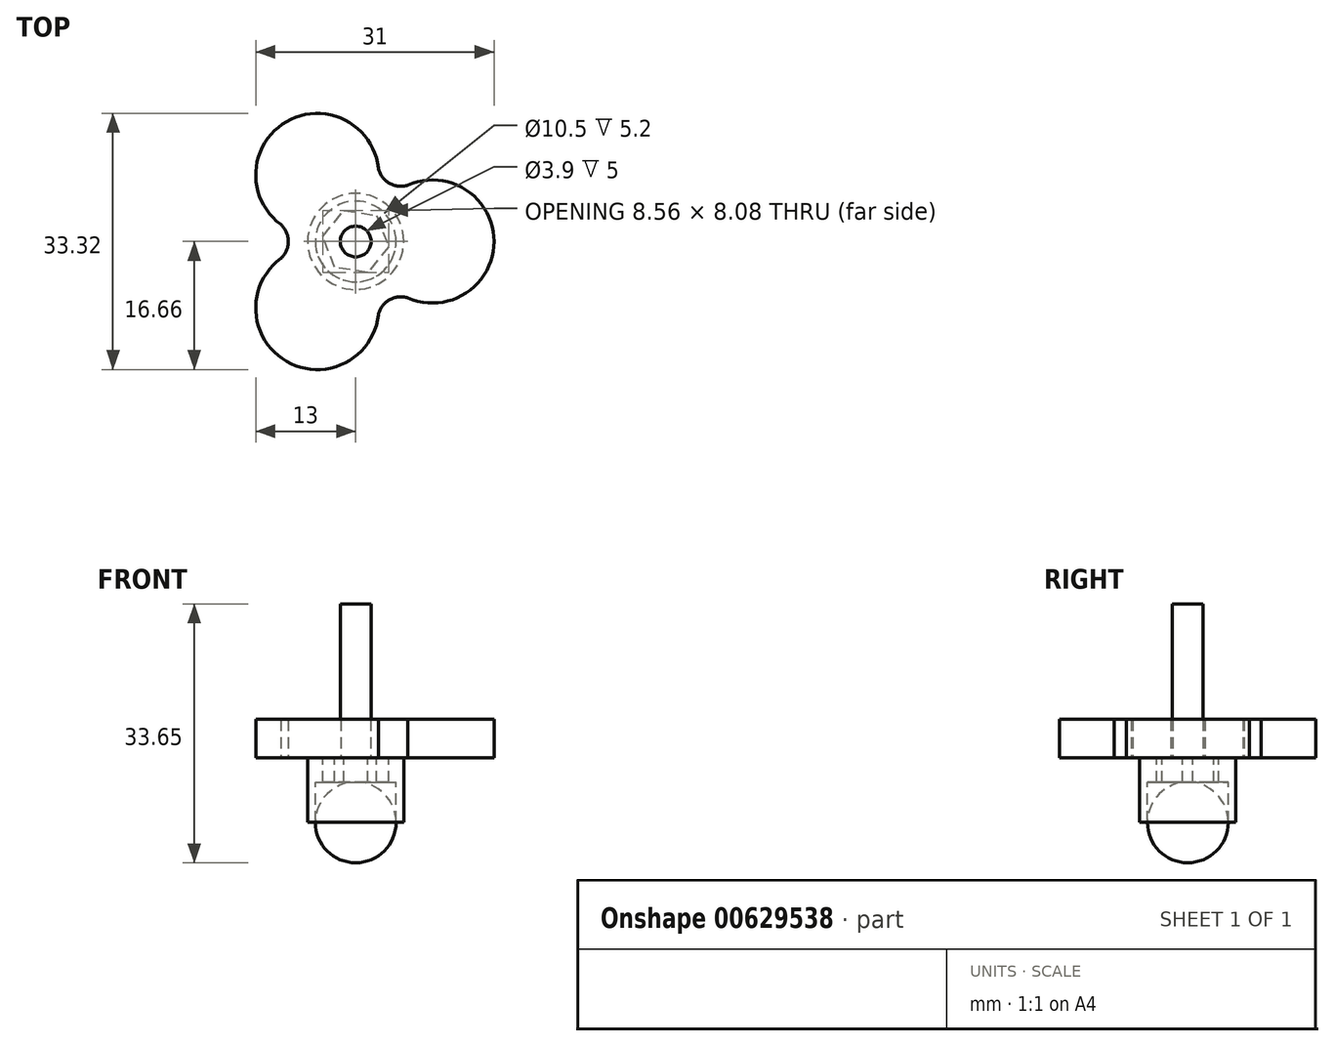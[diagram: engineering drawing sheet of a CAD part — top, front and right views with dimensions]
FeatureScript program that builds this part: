
annotation { "Feature Type Name" : "Feature", "Feature Type Description" : "" }
export const myFeature = defineFeature(function(context is Context, id is Id, definition is map)
    precondition{}
    {
        {
            var Q0;
            Q0=qCreatedBy(makeId("Top.planeOp"),FACE);
            var sketch = newSketch(context, id + "F0", { "sketchPlane" : qUnion([Q0])});
            skCircle(sketch, "E0", {"center": v(0, 0) * mm, "radius": 1.95 * mm});
            skArc(sketch, "E1", {"start": v(6.8, -7.33) * mm, "mid": v(18, 0) * mm, "end": v(6.8, 7.33) * mm});
            skArc(sketch, "E2", {"start": v(-9.75, -2.22) * mm, "mid": v(-9, -15.59) * mm, "end": v(2.95, -9.56) * mm});
            skArc(sketch, "E3.trimOffspring", {"start": v(2.95, 9.56) * mm, "mid": v(-9, 15.59) * mm, "end": v(-9.75, 2.22) * mm});
            skPoint(sketch, "E4", {"position": v(18, 0) * mm});
            skPoint(sketch, "E5", {"position": v(-9, 15.59) * mm});
            skPoint(sketch, "E6", {"position": v(-9, -15.59) * mm});
            skArc(sketch, "E7", {"start": v(-9.75, -2.22) * mm, "mid": v(-8.76, 0) * mm, "end": v(-9.75, 2.22) * mm});
            skArc(sketch, "E8", {"start": v(2.95, 9.56) * mm, "mid": v(4.38, 7.6) * mm, "end": v(6.8, 7.33) * mm});
            skArc(sketch, "E9", {"start": v(6.8, -7.33) * mm, "mid": v(4.38, -7.6) * mm, "end": v(2.95, -9.56) * mm});
            skSolve(sketch);
        }
        {
            var Q0;
            Q0 = qSketchRegion(id + "F0", true);
            extrude(context, id + "F1", {"entities" : qUnion([Q0]), "depth" : 5 * mm, "offsetDistance" : 25 * mm});
        }
        {
            var Q0;
            Q0=qCreatedBy(makeId("Top.planeOp"),FACE);
            var sketch = newSketch(context, id + "F2", { "sketchPlane" : qUnion([Q0])});
            skPoint(sketch, "E10.0.midPoint", {"position": v(2.46, -3.41) * mm});
            skCircle(sketch, "E11", {"center": v(0, 0) * mm, "radius": 6.25 * mm});
            skLineSegment(sketch, "E12.0", {"start": v(2.72, 3.37) * mm, "end": v(4.28, -0.67) * mm});
            skLineSegment(sketch, "E12.1", {"start": v(4.28, -0.67) * mm, "end": v(1.56, -4.04) * mm});
            skLineSegment(sketch, "E12.2", {"start": v(1.56, -4.04) * mm, "end": v(-2.72, -3.37) * mm});
            skLineSegment(sketch, "E12.3", {"start": v(-2.72, -3.37) * mm, "end": v(-4.28, 0.67) * mm});
            skLineSegment(sketch, "E12.4", {"start": v(-4.28, 0.67) * mm, "end": v(-1.56, 4.04) * mm});
            skLineSegment(sketch, "E12.5", {"start": v(-1.56, 4.04) * mm, "end": v(2.72, 3.37) * mm});
            skPoint(sketch, "E12.0.midPoint", {"position": v(3.5, 1.35) * mm});
            skSolve(sketch);
        }
        {
            var Q0;
            Q0 = qSketchRegion(id + "F2", true);
            extrude(context, id + "F3", {"entities" : qUnion([Q0]), "oppositeDirection" : true, "depth" : 3.2 * mm, "offsetDistance" : 25 * mm});
        }
        {
            var Q0;
            Q0=makeQuery(id+"F3.opExtrude","CAP_FACE",FACE,{"disambiguationData":[OSD([sQuery(id+"F2.wireOp",EDGE,"E10.0"),sQuery(id+"F2.wireOp",EDGE,"E10.1"),sQuery(id+"F2.wireOp",EDGE,"E10.2"),sQuery(id+"F2.wireOp",EDGE,"E10.3"),sQuery(id+"F2.wireOp",EDGE,"E10.4"),sQuery(id+"F2.wireOp",EDGE,"E10.5"),sQuery(id+"F2.wireOp",EDGE,"E11")])],"isStart":false});
            var sketch = newSketch(context, id + "F4", { "sketchPlane" : qUnion([Q0])});
            skCircle(sketch, "E13", {"center": v(0, 0) * mm, "radius": 5.25 * mm});
            skSolve(sketch);
        }
        {
            var Q0;
            Q0=makeQuery(id+"F4.imprint","IMPRINT",FACE,{"disambiguationData":[TD([[makeQuery(id+"F4.imprint","IMPRINT",EDGE,{"derivedFrom":sQuery(id+"F4.wireOp",EDGE,"E13")}),-1.0]])]});
            extrude(context, id + "F5", {"entities" : qUnion([Q0]), "operationType" : NewBodyOperationType.ADD, "depth" : 5.2 * mm, "offsetDistance" : 25 * mm});
        }
        {
            var Q0;
            Q0=makeQuery(id+"F1.opExtrude","CAP_FACE",FACE,{"disambiguationData":[OSD([sQuery(id+"F0.wireOp",EDGE,"E0"),sQuery(id+"F0.wireOp",EDGE,"E1"),sQuery(id+"F0.wireOp",EDGE,"E2"),sQuery(id+"F0.wireOp",EDGE,"E3.trimOffspring"),sQuery(id+"F0.wireOp",EDGE,"E7"),sQuery(id+"F0.wireOp",EDGE,"E8"),sQuery(id+"F0.wireOp",EDGE,"E9")])],"isStart":false});
            var sketch = newSketch(context, id + "F6", { "sketchPlane" : qUnion([Q0])});
            skCircle(sketch, "E14", {"center": v(0, 0) * mm, "radius": 2 * mm});
            skSolve(sketch);
        }
        {
            var Q0;
            Q0 = qSketchRegion(id + "F6", true);
            extrude(context, id + "F7", {"entities" : qUnion([Q0]), "operationType" : NewBodyOperationType.ADD, "depth" : 15 * mm, "offsetDistance" : 25 * mm});
        }
        {
            var Q0;
            Q0=makeQuery(id+"F5.opExtrude","CAP_FACE",FACE,{"disambiguationData":[OSD([sQuery(id+"F2.wireOp",EDGE,"E11"),sQuery(id+"F4.wireOp",EDGE,"E13")])],"isStart":false});
            var sketch = newSketch(context, id + "F8", { "sketchPlane" : qUnion([Q0])});
            skLineSegment(sketch, "E15", {"start": v(-5.25, 0) * mm, "end": v(5.25, 0) * mm});
            skArc(sketch, "E16", {"start": v(5.25, 0) * mm, "mid": v(0, 5.25) * mm, "end": v(-5.25, 0) * mm});
            skSolve(sketch);
        }
        {
            var Q0;
            Q0=makeQuery(id+"F8.imprint","IMPRINT",FACE,{"disambiguationData":[TD([[makeQuery(id+"F8.imprint","IMPRINT",EDGE,{"derivedFrom":sQuery(id+"F8.wireOp",EDGE,"E15")}),1.0]])]});
            var Q1;
            Q1=sQuery(id+"F8.wireOp",EDGE,"E15");
            revolve(context, id + "F9", {"entities" : qUnion([Q0]), "axis" : qUnion([Q1]), "revolveType" : RevolveType.FULL});
        }
    });
